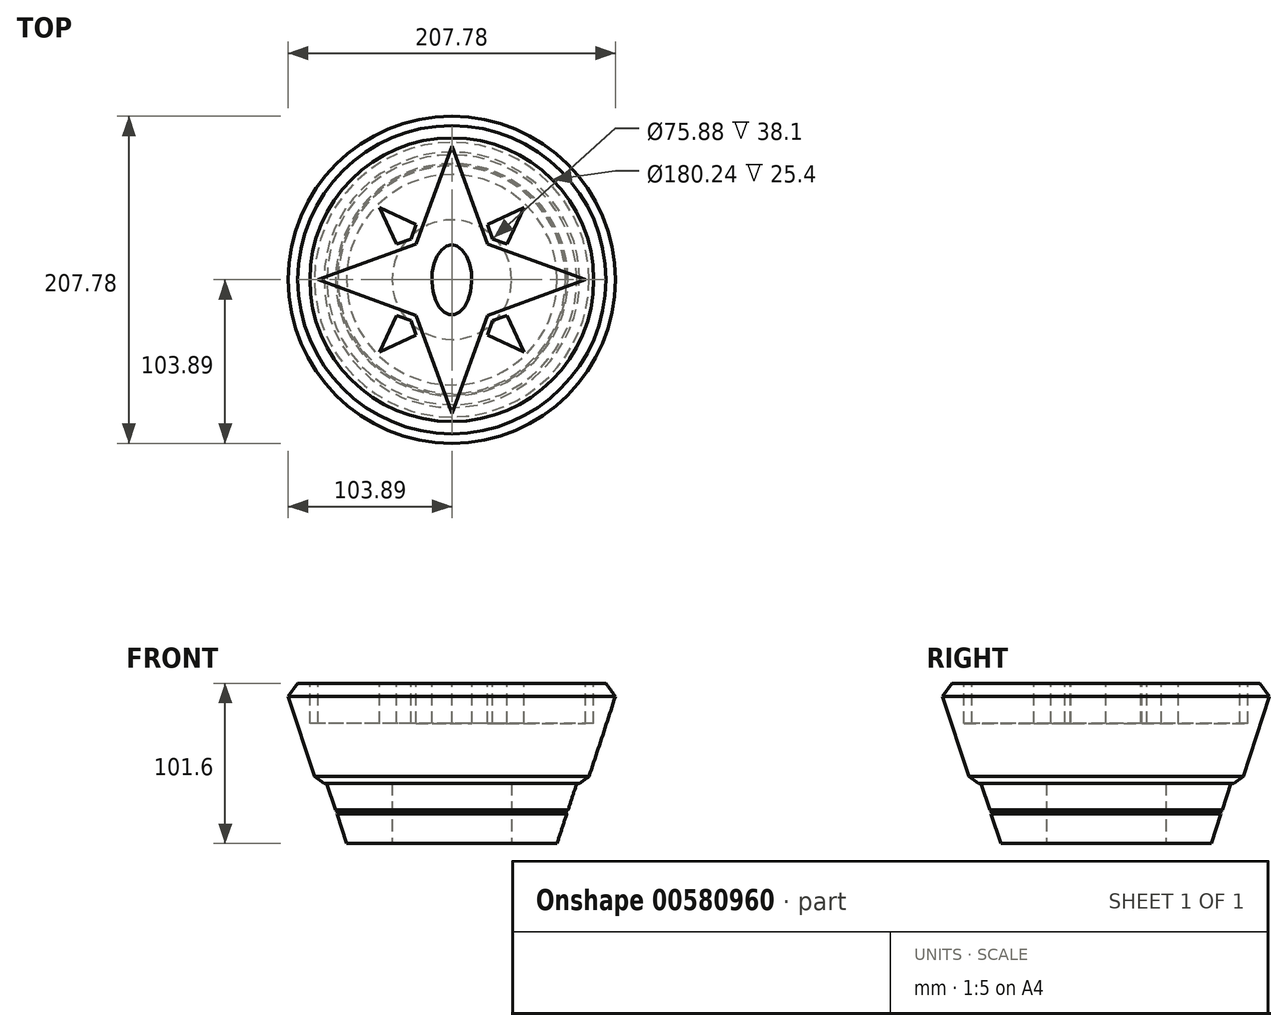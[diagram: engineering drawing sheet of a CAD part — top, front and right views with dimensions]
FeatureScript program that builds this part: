
annotation { "Feature Type Name" : "Feature", "Feature Type Description" : "" }
export const myFeature = defineFeature(function(context is Context, id is Id, definition is map)
    precondition{}
    {
        {
            var Q0;
            Q0=qCreatedBy(makeId("Top.planeOp"),FACE);
            var sketch = newSketch(context, id + "F0", { "sketchPlane" : qUnion([Q0])});
            skCircle(sketch, "E0", {"center": v(0, 0) * mm, "radius": 66.85 * mm});
            skSolve(sketch);
        }
        {
            var Q0;
            Q0=qCreatedBy(makeId("Top.planeOp"),FACE);
            cPlane(context, id + "F1", {"entities" : qUnion([Q0]), "cplaneType" : CPlaneType.OFFSET, "offset" : 101.6 * mm, "width" : 152.4 * mm, "height" : 152.4 * mm});
        }
        {
            var Q0;
            Q0=qCreatedBy(id+"F1.planeOp",FACE);
            var sketch = newSketch(context, id + "F2", { "sketchPlane" : qUnion([Q0])});
            skCircle(sketch, "E1", {"center": v(0, 0) * mm, "radius": 100.28 * mm});
            skSolve(sketch);
        }
        {
            var Q0;
            Q0=makeQuery(id+"F2.imprint","IMPRINT",FACE,{"disambiguationData":[TD([[makeQuery(id+"F2.imprint","IMPRINT",EDGE,{"derivedFrom":sQuery(id+"F2.wireOp",EDGE,"E1")}),1.0]])]});
            var Q1;
            Q1=makeQuery(id+"F0.imprint","IMPRINT",FACE,{"disambiguationData":[TD([[makeQuery(id+"F0.imprint","IMPRINT",EDGE,{"derivedFrom":sQuery(id+"F0.wireOp",EDGE,"E0")}),1.0]])]});
            var Q2;
            Q2=sQuery(id+"F2.wireOp",EDGE,"Eyu8YDiN-lEGU-Wuxt-0ncA-RZLAWeJK4OgB");
            var Q3;
            Q3=sQuery(id+"F0.wireOp",EDGE,"fgfE4CqQ-t5n6-ucAx-yhIW-5wF2yx0Jya2k");
            loft(context, id + "F3", {"sheetProfilesArray" : [{ "sheetProfileEntities" : qUnion([Q0]) }, { "sheetProfileEntities" : qUnion([Q1]) }], "wireProfilesArray" : [{ "wireProfileEntities" : qUnion([Q2]) }, { "wireProfileEntities" : qUnion([Q3]) }]});
        }
        {
            var Q0;
            Q0=qCreatedBy(makeId("Top.planeOp"),FACE);
            var sketch = newSketch(context, id + "F4", { "sketchPlane" : qUnion([Q0])});
            skCircle(sketch, "E2", {"center": v(0, 0) * mm, "radius": 37.94 * mm});
            skSolve(sketch);
        }
        {
            var Q0;
            Q0=makeQuery(id+"F4.imprint","IMPRINT",FACE,{"disambiguationData":[TD([[makeQuery(id+"F4.imprint","IMPRINT",EDGE,{"derivedFrom":sQuery(id+"F4.wireOp",EDGE,"E2")}),1.0]])]});
            extrude(context, id + "F5", {"entities" : qUnion([Q0]), "operationType" : NewBodyOperationType.REMOVE, "depth" : 53.34 * mm, "offsetDistance" : 25.4 * mm});
        }
        {
            var Q0;
            Q0=qCreatedBy(makeId("Top.planeOp"),FACE);
            cPlane(context, id + "F6", {"entities" : qUnion([Q0]), "cplaneType" : CPlaneType.OFFSET, "offset" : 38.1 * mm, "width" : 152.4 * mm, "height" : 152.4 * mm});
        }
        {
            var Q0;
            Q0=qCreatedBy(id+"F6.planeOp",FACE);
            var sketch = newSketch(context, id + "F7", { "sketchPlane" : qUnion([Q0])});
            skCircle(sketch, "E3", {"center": v(0, 0) * mm, "radius": 85.73 * mm});
            skSolve(sketch);
        }
        {
            var Q0;
            Q0=qCreatedBy(id+"F1.planeOp",FACE);
            var sketch = newSketch(context, id + "F8", { "sketchPlane" : qUnion([Q0])});
            skCircle(sketch, "E4", {"center": v(0, 0) * mm, "radius": 106.63 * mm});
            skSolve(sketch);
        }
        {
            var Q1;
            Q1=makeQuery(id+"F7.imprint","IMPRINT",FACE,{"disambiguationData":[TD([[makeQuery(id+"F7.imprint","IMPRINT",EDGE,{"derivedFrom":sQuery(id+"F7.wireOp",EDGE,"E3")}),1.0]])]});
            var Q2;
            Q2=makeQuery(id+"F8.imprint","IMPRINT",FACE,{"disambiguationData":[TD([[makeQuery(id+"F8.imprint","IMPRINT",EDGE,{"derivedFrom":sQuery(id+"F8.wireOp",EDGE,"E4")}),1.0]])]});
            loft(context, id + "F9", {"operationType" : NewBodyOperationType.ADD, "sheetProfilesArray" : [{ "sheetProfileEntities" : qUnion([Q1]) }, { "sheetProfileEntities" : qUnion([Q2]) }]});
        }
        {
            var Q0;
            Q0=makeQuery(id+"F9.opLoft","MID_CAP_EDGE",EDGE,{"disambiguationData":[OSD([sQuery(id+"F7.wireOp",EDGE,"E3")])],"capPos":0.0});
            chamfer(context, id + "F10", {"entities" : qUnion([Q0]), "width" : 6.35 * mm, "tangentPropagation" : true});
        }
        {
            var Q0;
            Q0=makeQuery(id+"F9.opLoft","MID_CAP_EDGE",EDGE,{"disambiguationData":[OSD([sQuery(id+"F7.wireOp",EDGE,"E3"),sQuery(id+"F8.wireOp",EDGE,"E4")])],"capPos":1.0});
            chamfer(context, id + "F11", {"entities" : qUnion([Q0]), "width" : 6.35 * mm, "tangentPropagation" : true});
        }
        {
            var Q0;
            Q0=qCreatedBy(makeId("Front.planeOp"),FACE);
            var sketch = newSketch(context, id + "F12", { "sketchPlane" : qUnion([Q0])});
            skLineSegment(sketch, "E5", {"start": v(-79.4, 38.11) * mm, "end": v(-66.85, 0) * mm});
            skLineSegment(sketch, "E6", {"start": v(-73.8, 21.14) * mm, "end": v(-72.2, 20.33) * mm});
            skLineSegment(sketch, "E7", {"start": v(-72.2, 20.33) * mm, "end": v(-73.02, 18.73) * mm});
            skSolve(sketch);
        }
        {
            var Q0;
            Q0=qCreatedBy(makeId("Right.planeOp"),FACE);
            var sketch = newSketch(context, id + "F13", { "sketchPlane" : qUnion([Q0])});
            skLineSegment(sketch, "E8", {"start": v(0, 0) * mm, "end": v(0, 184.2) * mm});
            skSolve(sketch);
        }
        {
            var Q0;
            Q0=qSketchRegion(id+"F12",true);
            var Q1;
            Q1=sQuery(id+"F13.wireOp",EDGE,"E8");
            revolve(context, id + "F14", {"operationType" : NewBodyOperationType.REMOVE, "entities" : qUnion([Q0]), "axis" : qUnion([Q1]), "revolveType" : RevolveType.FULL, "oppositeDirection" : true});
        }
        {
            var Q0;
            Q0=makeQuery(id+"F9.boolean.opBoolean","MERGE",FACE,{"derivedFrom":[makeQuery(id+"F3.opLoft","CAP_FACE",FACE,{"disambiguationData":[OSD([makeQuery(id+"F2.imprint","IMPRINT",FACE,{"disambiguationData":[TD([[makeQuery(id+"F2.imprint","IMPRINT",EDGE,{"derivedFrom":sQuery(id+"F2.wireOp",EDGE,"E1")}),1.0]])]})])],"isStart":true}),makeQuery(id+"F9.opLoft","CAP_FACE",FACE,{"disambiguationData":[OSD([makeQuery(id+"F8.imprint","IMPRINT",FACE,{"disambiguationData":[TD([[makeQuery(id+"F8.imprint","IMPRINT",EDGE,{"derivedFrom":sQuery(id+"F8.wireOp",EDGE,"E4")}),1.0]])]})])],"isStart":true})]});
            var sketch = newSketch(context, id + "F15", { "sketchPlane" : qUnion([Q0])});
            skCircle(sketch, "E9", {"center": v(0, 0) * mm, "radius": 100.28 * mm});
            skCircle(sketch, "E10.0", {"center": v(0, 0) * mm, "radius": 90.12 * mm});
            skEllipse(sketch, "E11", {"center": v(0, 0) * mm, "majorRadius": 22.23 * mm, "minorRadius": 12.7 * mm, "majorAxis": v(0, 1)});
            skLineSegment(sketch, "E12", {"start": v(-22.7, 22.7) * mm, "end": v(0, 85.04) * mm});
            skLineSegment(sketch, "E13", {"start": v(-22.7, 22.7) * mm, "end": v(-85.04, 0) * mm});
            skLineSegment(sketch, "E14", {"start": v(0, 0) * mm, "end": v(7.61, 0) * mm});
            skLineSegment(sketch, "E15", {"start": v(0, 0) * mm, "end": v(0, 8.13) * mm});
            skLineSegment(sketch, "E16", {"start": v(0, 0) * mm, "end": v(-22.7, 22.7) * mm});
            skLineSegment(sketch, "E17", {"start": v(-26, 26) * mm, "end": v(-35.07, 22.7) * mm});
            skLineSegment(sketch, "E18", {"start": v(-35.07, 22.7) * mm, "end": v(-45.88, 45.88) * mm});
            skLineSegment(sketch, "E19", {"start": v(-45.88, 45.88) * mm, "end": v(-22.7, 35.07) * mm});
            skLineSegment(sketch, "E20", {"start": v(-22.7, 35.07) * mm, "end": v(-26, 26) * mm});
            skLineSegment(sketch, "E21.1.0", {"start": v(-22.7, -22.7) * mm, "end": v(0, -85.04) * mm});
            skLineSegment(sketch, "E21.1.1", {"start": v(-22.7, -35.07) * mm, "end": v(-45.88, -45.88) * mm});
            skLineSegment(sketch, "E21.1.2", {"start": v(-45.88, -45.88) * mm, "end": v(-35.07, -22.7) * mm});
            skLineSegment(sketch, "E21.1.3", {"start": v(-35.07, -22.7) * mm, "end": v(-26, -26) * mm});
            skLineSegment(sketch, "E21.1.4", {"start": v(-26, -26) * mm, "end": v(-22.7, -35.07) * mm});
            skLineSegment(sketch, "E21.1.5", {"start": v(-22.7, -22.7) * mm, "end": v(-85.04, 0) * mm});
            skLineSegment(sketch, "E21.2.0", {"start": v(22.7, -22.7) * mm, "end": v(85.04, 0) * mm});
            skLineSegment(sketch, "E21.2.1", {"start": v(35.07, -22.7) * mm, "end": v(45.88, -45.88) * mm});
            skLineSegment(sketch, "E21.2.2", {"start": v(45.88, -45.88) * mm, "end": v(22.7, -35.07) * mm});
            skLineSegment(sketch, "E21.2.3", {"start": v(22.7, -35.07) * mm, "end": v(26, -26) * mm});
            skLineSegment(sketch, "E21.2.4", {"start": v(26, -26) * mm, "end": v(35.07, -22.7) * mm});
            skLineSegment(sketch, "E21.2.5", {"start": v(22.7, -22.7) * mm, "end": v(0, -85.04) * mm});
            skLineSegment(sketch, "E21.3.0", {"start": v(22.7, 22.7) * mm, "end": v(0, 85.04) * mm});
            skLineSegment(sketch, "E21.3.1", {"start": v(22.7, 35.07) * mm, "end": v(45.88, 45.88) * mm});
            skLineSegment(sketch, "E21.3.2", {"start": v(45.88, 45.88) * mm, "end": v(35.07, 22.7) * mm});
            skLineSegment(sketch, "E21.3.3", {"start": v(35.07, 22.7) * mm, "end": v(26, 26) * mm});
            skLineSegment(sketch, "E21.3.4", {"start": v(26, 26) * mm, "end": v(22.7, 35.07) * mm});
            skLineSegment(sketch, "E21.3.5", {"start": v(22.7, 22.7) * mm, "end": v(85.04, 0) * mm});
            skSolve(sketch);
        }
        {
            var Q0;
            {var subQ0=sQuery(id+"F15.wireOp",EDGE,"2d981b6a-a36c-429e-8e7e-1961ac6362790.MirrorCS");var subQ1=sQuery(id+"F15.wireOp",EDGE,"K4UFzg29-vVcX-KDtk-gjHo-bnuy8YvNwfuU");var subQ2=makeQuery(id+"F15.imprint","INTERSECT",VERTEX,{"derivedFrom":[subQ1,subQ0]});Q0=makeQuery(id+"F15.imprint","IMPRINT",FACE,{"disambiguationData":[TD([[makeQuery(id+"F15.imprint","IMPRINT",EDGE,{"disambiguationData":[TD([[subQ2,-1.0]])],"derivedFrom":subQ1}),-1.0]])]});}
            var Q1;
            Q1=makeQuery(id+"F15.imprint","IMPRINT",FACE,{"disambiguationData":[TD([[makeQuery(id+"F15.imprint","IMPRINT",EDGE,{"derivedFrom":sQuery(id+"F15.wireOp",EDGE,"E10.0")}),1.0]])]});
            var Q2;
            Q2=makeQuery(id+"F15.imprint","IMPRINT",FACE,{"disambiguationData":[TD([[makeQuery(id+"F15.imprint","IMPRINT",EDGE,{"derivedFrom":sQuery(id+"F15.wireOp",EDGE,"3ecf9a04-cdc3-40a6-907b-ea063ad2b2e0.0")}),1.0]])]});
            var Q3;
            {var subQ0=sQuery(id+"F15.wireOp",EDGE,"f71a98ee-37c5-4e0d-85ec-4346386b53170.MirrorCS");var subQ1=sQuery(id+"F15.wireOp",EDGE,"K4UFzg29-vVcX-KDtk-gjHo-bnuy8YvNwfuU");var subQ2=makeQuery(id+"F15.imprint","INTERSECT",VERTEX,{"derivedFrom":[subQ1,subQ0]});Q3=makeQuery(id+"F15.imprint","IMPRINT",FACE,{"disambiguationData":[TD([[makeQuery(id+"F15.imprint","IMPRINT",EDGE,{"disambiguationData":[TD([[subQ2,-1.0]])],"derivedFrom":subQ1}),-1.0]])]});}
            var Q4;
            Q4=makeQuery(id+"F15.imprint","IMPRINT",FACE,{"disambiguationData":[TD([[makeQuery(id+"F15.imprint","IMPRINT",EDGE,{"derivedFrom":sQuery(id+"F15.wireOp",EDGE,"E11")}),1.0]])]});
            extrude(context, id + "F16", {"entities" : qUnion([Q0, Q1, Q2, Q3, Q4]), "operationType" : NewBodyOperationType.REMOVE, "oppositeDirection" : true, "depth" : 25.4 * mm, "offsetDistance" : 25.4 * mm});
        }
    });
